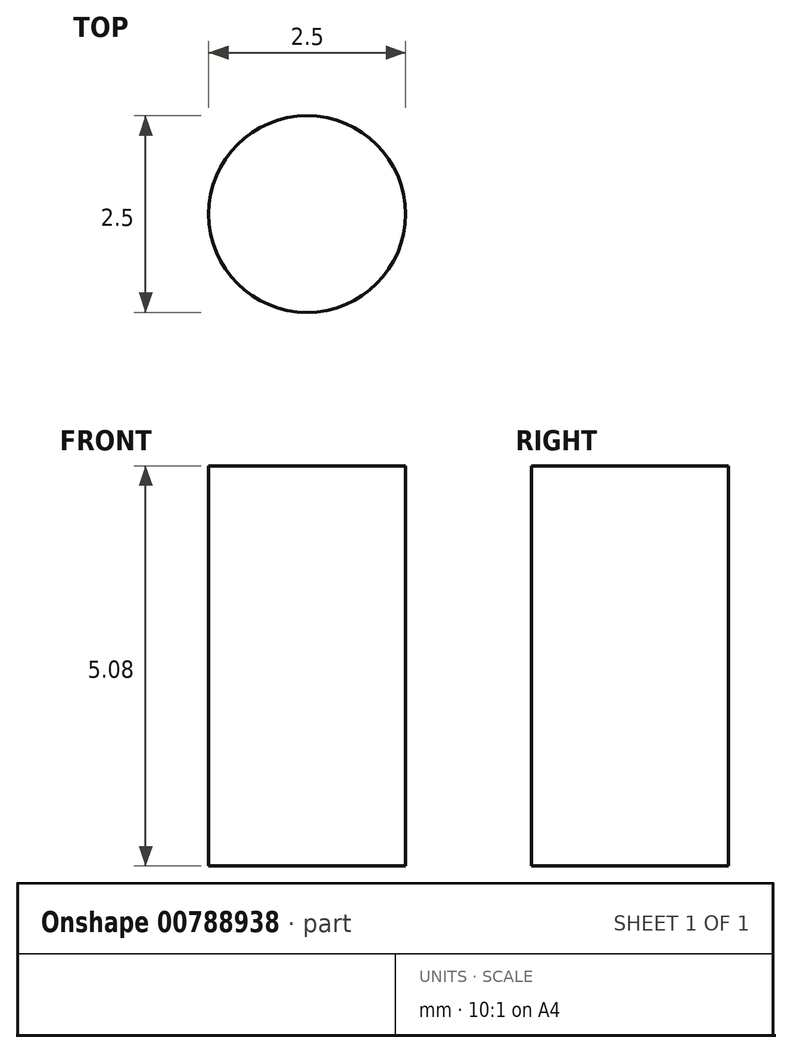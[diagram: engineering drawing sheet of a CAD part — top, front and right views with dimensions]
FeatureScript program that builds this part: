
annotation { "Feature Type Name" : "Feature", "Feature Type Description" : "" }
export const myFeature = defineFeature(function(context is Context, id is Id, definition is map)
    precondition{}
    {
        {
            var Q0;
            Q0=qCreatedBy(makeId("Top.planeOp"),FACE);
            var sketch = newSketch(context, id + "F0", { "sketchPlane" : qUnion([Q0])});
            skCircle(sketch, "E0", {"center": v(0, 0) * mm, "radius": 1.25 * mm});
            skSolve(sketch);
        }
        {
            var Q0;
            Q0=makeQuery(id+"F0.imprint","IMPRINT",FACE,{"disambiguationData":[TD([[makeQuery(id+"F0.imprint","IMPRINT",EDGE,{"derivedFrom":sQuery(id+"F0.wireOp",EDGE,"E0")}),1.0]])]});
            extrude(context, id + "F1", {"entities" : qUnion([Q0]), "depth" : 5.08 * mm, "offsetDistance" : 25.4 * mm});
        }
    });
